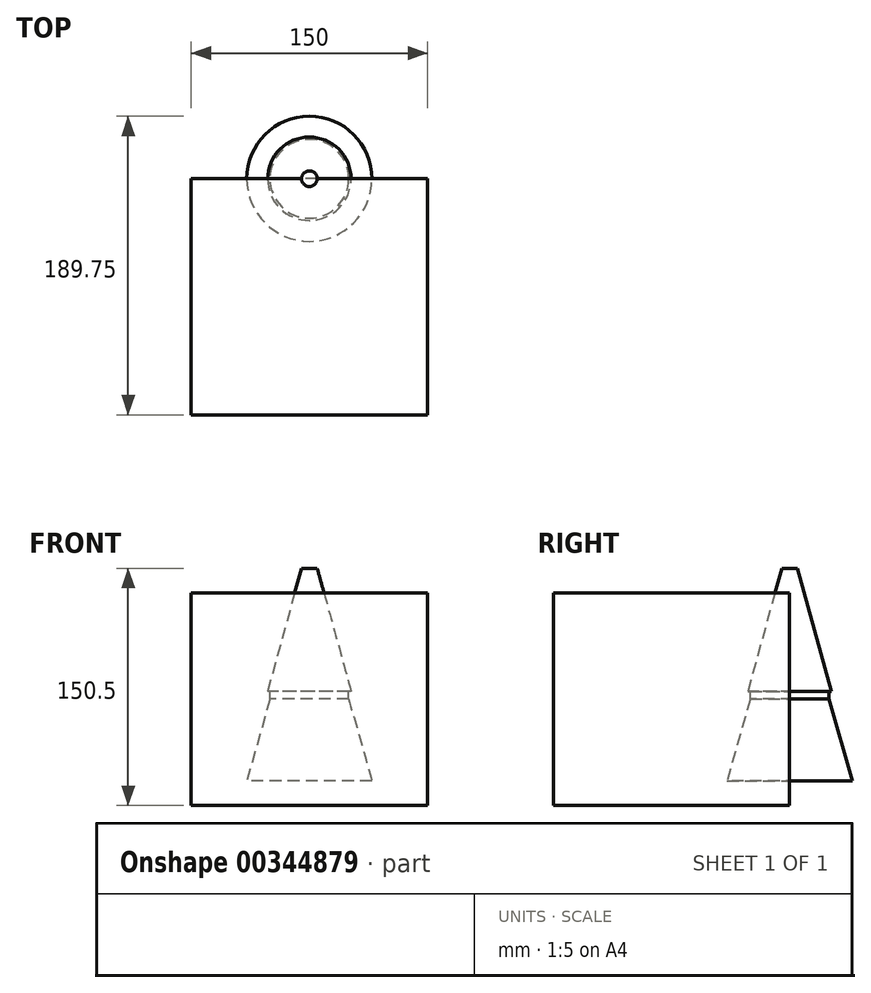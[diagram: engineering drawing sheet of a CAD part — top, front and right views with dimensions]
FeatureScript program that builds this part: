
annotation { "Feature Type Name" : "Feature", "Feature Type Description" : "" }
export const myFeature = defineFeature(function(context is Context, id is Id, definition is map)
    precondition{}
    {
        {
            var Q0;
            Q0=qCreatedBy(makeId("Front.planeOp"),FACE);
            var sketch = newSketch(context, id + "F0", { "sketchPlane" : qUnion([Q0])});
            skLineSegment(sketch, "E0", {"start": v(0, 83) * mm, "end": v(5, 83) * mm});
            skLineSegment(sketch, "E1", {"start": v(0, 83) * mm, "end": v(0, -52) * mm});
            skLineSegment(sketch, "E2", {"start": v(0, 83) * mm, "end": v(0, 0) * mm});
            skLineSegment(sketch, "E3", {"start": v(0, -52) * mm, "end": v(39.75, -52) * mm});
            skLineSegment(sketch, "E4", {"start": v(25, 0) * mm, "end": v(39.75, -52) * mm});
            skLineSegment(sketch, "E5", {"start": v(25, 0) * mm, "end": v(25, 5) * mm});
            skLineSegment(sketch, "E6", {"start": v(25, 5) * mm, "end": v(26.5, 5) * mm});
            skLineSegment(sketch, "E7", {"start": v(5, 83) * mm, "end": v(26.5, 5) * mm});
            skSolve(sketch);
        }
        {
            var Q0;
            Q0=makeQuery(id+"F0.imprint","IMPRINT",FACE,{"disambiguationData":[TD([[makeQuery(id+"F0.imprint","IMPRINT",EDGE,{"derivedFrom":sQuery(id+"F0.wireOp",EDGE,"E0")}),-1.0]])]});
            var Q1;
            Q1=sQuery(id+"F0.wireOp",EDGE,"E2");
            revolve(context, id + "F1", {"entities" : qUnion([Q0]), "axis" : qUnion([Q1]), "revolveType" : RevolveType.FULL});
        }
        {
            var Q0;
            Q0=qCreatedBy(makeId("Front.planeOp"),FACE);
            var sketch = newSketch(context, id + "F2", { "sketchPlane" : qUnion([Q0])});
            skLineSegment(sketch, "E8.bottom", {"start": v(75, -67.5) * mm, "end": v(-75, -67.5) * mm});
            skLineSegment(sketch, "E8.top", {"start": v(75, 67.5) * mm, "end": v(-75, 67.5) * mm});
            skLineSegment(sketch, "E8.left", {"start": v(75, -67.5) * mm, "end": v(75, 67.5) * mm});
            skLineSegment(sketch, "E8.right", {"start": v(-75, -67.5) * mm, "end": v(-75, 67.5) * mm});
            skPoint(sketch, "E8.middle", {"position": v(0, 0) * mm});
            skSolve(sketch);
        }
        {
            var Q0;
            Q0 = qSketchRegion(id + "F2", true);
            extrude(context, id + "F3", {"entities" : qUnion([Q0]), "depth" : 150 * mm});
        }
    });
